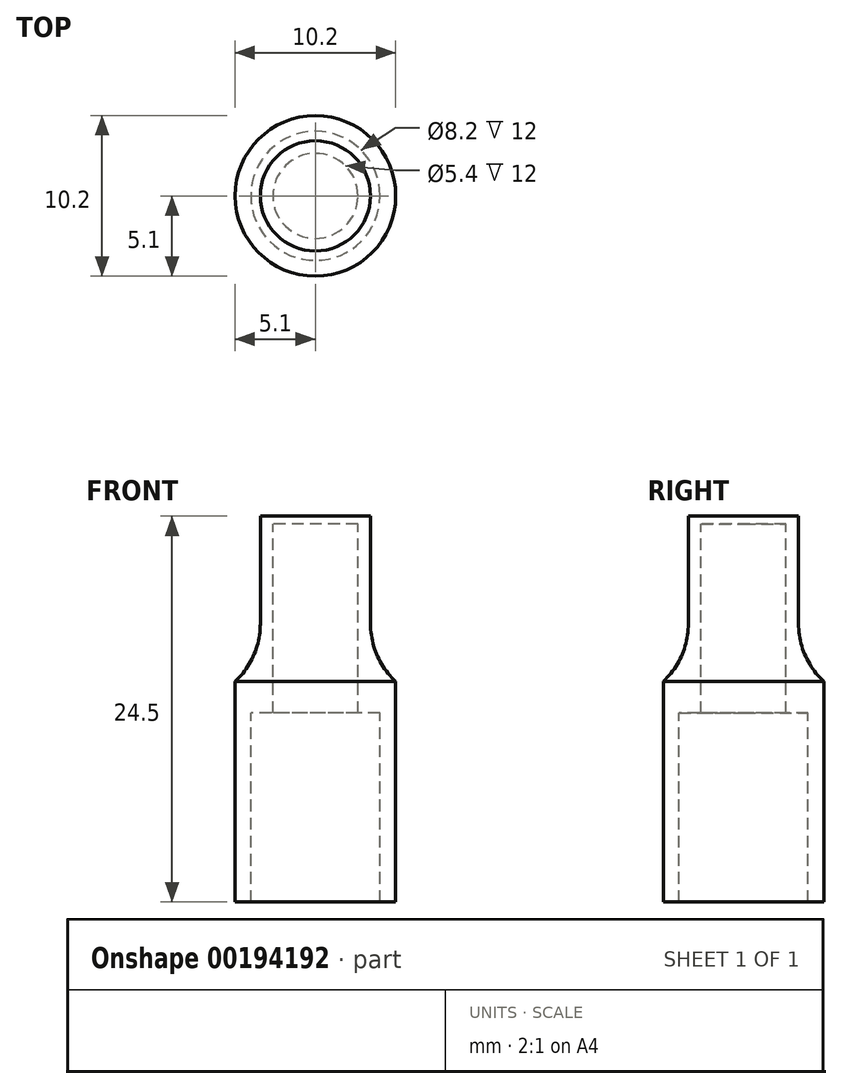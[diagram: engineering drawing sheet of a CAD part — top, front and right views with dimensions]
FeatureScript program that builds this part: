
annotation { "Feature Type Name" : "Feature", "Feature Type Description" : "" }
export const myFeature = defineFeature(function(context is Context, id is Id, definition is map)
    precondition{}
    {
        {
            var Q0;
            Q0=qCreatedBy(makeId("Front.planeOp"),FACE);
            var sketch = newSketch(context, id + "F0", { "sketchPlane" : qUnion([Q0])});
            skLineSegment(sketch, "E0", {"start": v(5.1, -14) * mm, "end": v(5.1, 0) * mm});
            skLineSegment(sketch, "E1", {"start": v(5.1, 0) * mm, "end": v(3.5, 0) * mm});
            skLineSegment(sketch, "E2", {"start": v(3.5, 0) * mm, "end": v(3.5, 10.5) * mm});
            skLineSegment(sketch, "E3", {"start": v(4.1, -14) * mm, "end": v(5.1, -14) * mm});
            skLineSegment(sketch, "E4", {"start": v(4.1, -14) * mm, "end": v(4.1, -2) * mm});
            skLineSegment(sketch, "E5", {"start": v(4.1, -2) * mm, "end": v(2.7, -2) * mm});
            skLineSegment(sketch, "E6", {"start": v(2.7, 10) * mm, "end": v(2.7, -2) * mm});
            skLineSegment(sketch, "E7", {"start": v(0, 10.5) * mm, "end": v(0, 10) * mm});
            skLineSegment(sketch, "E8", {"start": v(0, 10) * mm, "end": v(2.7, 10) * mm});
            skLineSegment(sketch, "E9", {"start": v(0, 10.5) * mm, "end": v(3.5, 10.5) * mm});
            skLineSegment(sketch, "E10", {"start": v(0, 12.15) * mm, "end": v(0, -25.72) * mm, "construction": true});
            skSolve(sketch);
        }
        {
            var Q0;
            Q0=makeQuery(id+"F0.imprint","IMPRINT",FACE,{"disambiguationData":[TD([[makeQuery(id+"F0.imprint","IMPRINT",EDGE,{"derivedFrom":sQuery(id+"F0.wireOp",EDGE,"E0")}),1.0]])]});
            var Q1;
            Q1=sQuery(id+"F0.wireOp",EDGE,"E10");
            revolve(context, id + "F1", {"entities" : qUnion([Q0]), "axis" : qUnion([Q1]), "revolveType" : RevolveType.FULL});
        }
        {
            var Q0;
            Q0=makeQuery(id+"F1.opRevolve","SWEPT_EDGE",EDGE,{"disambiguationData":[OSD([sQuery(id+"F0.wireOp",EDGE,"E1"),sQuery(id+"F0.wireOp",EDGE,"E2")])]});
            fillet(context, id + "F2", {"entities" : qUnion([Q0]), "radius" : 5 * mm, "tangentPropagation" : true, "allowEdgeOverflow" : false});
        }
    });
